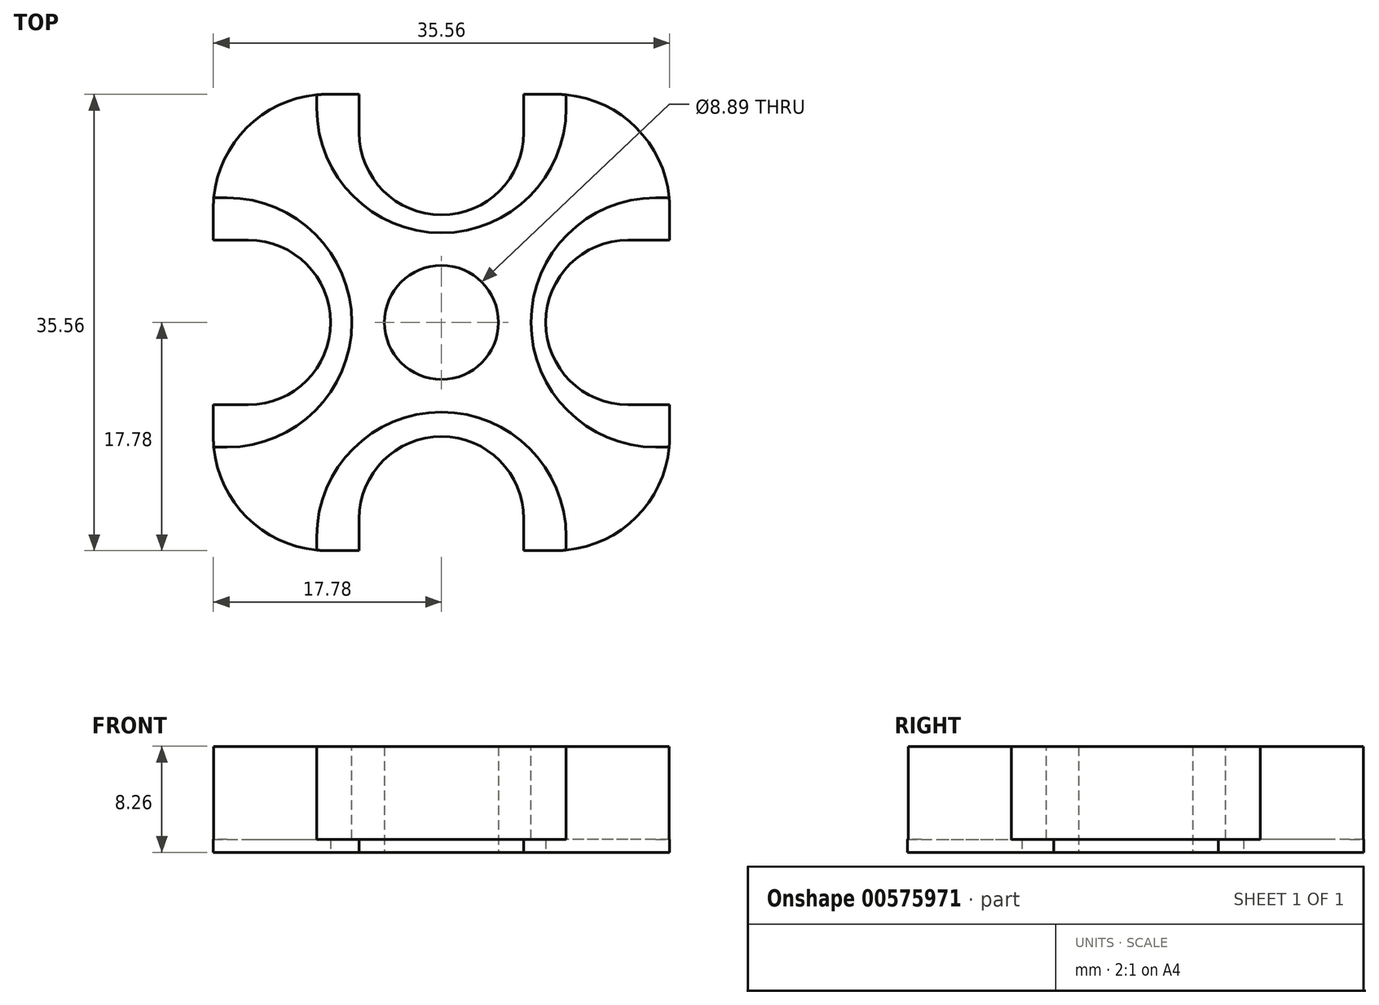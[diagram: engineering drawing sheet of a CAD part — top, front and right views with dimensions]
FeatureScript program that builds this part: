
annotation { "Feature Type Name" : "Feature", "Feature Type Description" : "" }
export const myFeature = defineFeature(function(context is Context, id is Id, definition is map)
    precondition{}
    {
        {
            var Q0;
            Q0=qCreatedBy(makeId("Top.planeOp"),FACE);
            var sketch = newSketch(context, id + "F0", { "sketchPlane" : qUnion([Q0])});
            skLineSegment(sketch, "E0.bottom", {"start": v(17.78, -17.78) * mm, "end": v(-17.78, -17.78) * mm});
            skLineSegment(sketch, "E0.top", {"start": v(17.78, 17.78) * mm, "end": v(-17.78, 17.78) * mm});
            skLineSegment(sketch, "E0.left", {"start": v(17.78, -17.78) * mm, "end": v(17.78, 17.78) * mm});
            skLineSegment(sketch, "E0.right", {"start": v(-17.78, -17.78) * mm, "end": v(-17.78, 17.78) * mm});
            skPoint(sketch, "E0.middle", {"position": v(0, 0) * mm});
            skArc(sketch, "E1", {"start": v(-8.14, -17.78) * mm, "mid": v(0, -23.06) * mm, "end": v(8.14, -17.78) * mm});
            skPoint(sketch, "E2.center.orphan", {"position": v(0, 15.65) * mm});
            skPoint(sketch, "E3.center.orphan", {"position": v(-13.58, 0) * mm});
            skPoint(sketch, "E4.center.orphan", {"position": v(13.88, 0) * mm});
            skSolve(sketch);
        }
        {
            var Q0;
            Q0=makeQuery(id+"F0.imprint","IMPRINT",FACE,{"disambiguationData":[TD([[makeQuery(id+"F0.imprint","IMPRINT",EDGE,{"derivedFrom":sQuery(id+"F0.wireOp",EDGE,"E0.top")}),1.0]])]});
            extrude(context, id + "F1", {"entities" : qUnion([Q0]), "depth" : 8.25 * mm, "offsetDistance" : 25.4 * mm});
        }
        {
            var Q0;
            Q0=makeQuery(id+"F1.opExtrude","CAP_FACE",FACE,{"disambiguationData":[OSD([sQuery(id+"F0.wireOp",EDGE,"E0.bottom"),sQuery(id+"F0.wireOp",EDGE,"E0.top"),sQuery(id+"F0.wireOp",EDGE,"E0.left"),sQuery(id+"F0.wireOp",EDGE,"E0.right")])],"isStart":false});
            var sketch = newSketch(context, id + "F2", { "sketchPlane" : qUnion([Q0])});
            skArc(sketch, "E5", {"start": v(-9.72, 16.7) * mm, "mid": v(0, 6.99) * mm, "end": v(9.72, 16.7) * mm});
            skArc(sketch, "E6", {"start": v(16.7, 9.72) * mm, "mid": v(6.98, 0) * mm, "end": v(16.7, -9.72) * mm});
            skArc(sketch, "E7", {"start": v(-16.7, -9.72) * mm, "mid": v(-6.99, 0) * mm, "end": v(-16.7, 9.72) * mm});
            skArc(sketch, "E8", {"start": v(9.72, -16.7) * mm, "mid": v(0, -6.99) * mm, "end": v(-9.72, -16.7) * mm});
            skLineSegment(sketch, "E9", {"start": v(-9.72, 16.7) * mm, "end": v(-9.72, 17.78) * mm});
            skLineSegment(sketch, "E10", {"start": v(9.72, 16.7) * mm, "end": v(9.72, 17.78) * mm});
            skLineSegment(sketch, "E11", {"start": v(-16.7, 9.72) * mm, "end": v(-17.78, 9.72) * mm});
            skLineSegment(sketch, "E12", {"start": v(-16.7, -9.72) * mm, "end": v(-17.78, -9.72) * mm});
            skLineSegment(sketch, "E13", {"start": v(-9.72, -16.7) * mm, "end": v(-9.72, -17.78) * mm});
            skLineSegment(sketch, "E14", {"start": v(9.72, -16.7) * mm, "end": v(9.72, -17.78) * mm});
            skLineSegment(sketch, "E15", {"start": v(16.7, 9.72) * mm, "end": v(17.78, 9.72) * mm});
            skLineSegment(sketch, "E16", {"start": v(16.7, -9.72) * mm, "end": v(17.78, -9.72) * mm});
            skPoint(sketch, "E17.orphan", {"position": v(-9.66, -17.78) * mm});
            skLineSegment(sketch, "E18", {"start": v(9.72, 17.78) * mm, "end": v(-9.72, 17.78) * mm});
            skLineSegment(sketch, "E19", {"start": v(-17.78, 9.72) * mm, "end": v(-17.78, -9.72) * mm});
            skLineSegment(sketch, "E20", {"start": v(17.78, -9.72) * mm, "end": v(17.78, 9.72) * mm});
            skLineSegment(sketch, "E21", {"start": v(-9.72, -17.78) * mm, "end": v(9.72, -17.78) * mm});
            skSolve(sketch);
        }
        {
            var Q0;
            Q0=qSketchRegion(id+"F2",true);
            extrude(context, id + "F3", {"entities" : qUnion([Q0]), "operationType" : NewBodyOperationType.REMOVE, "oppositeDirection" : true, "depth" : 7.24 * mm, "offsetDistance" : 25.4 * mm});
        }
        {
            var Q0;
            Q0=makeQuery(id+"F1.opExtrude","CAP_FACE",FACE,{"disambiguationData":[OSD([sQuery(id+"F0.wireOp",EDGE,"E0.bottom"),sQuery(id+"F0.wireOp",EDGE,"E0.top"),sQuery(id+"F0.wireOp",EDGE,"E0.left"),sQuery(id+"F0.wireOp",EDGE,"E0.right")])],"isStart":true});
            var sketch = newSketch(context, id + "F4", { "sketchPlane" : qUnion([Q0])});
            skArc(sketch, "E22", {"start": v(-6.41, 15.3) * mm, "mid": v(0, 8.9) * mm, "end": v(6.41, 15.3) * mm});
            skArc(sketch, "E23", {"start": v(14.54, 6.41) * mm, "mid": v(8.13, 0) * mm, "end": v(14.54, -6.41) * mm});
            skArc(sketch, "E24", {"start": v(-15.05, -6.41) * mm, "mid": v(-8.64, 0) * mm, "end": v(-15.05, 6.41) * mm});
            skArc(sketch, "E25", {"start": v(6.41, -14.8) * mm, "mid": v(0, -8.38) * mm, "end": v(-6.41, -14.8) * mm});
            skLineSegment(sketch, "E26", {"start": v(-15.05, 6.41) * mm, "end": v(-17.78, 6.41) * mm});
            skLineSegment(sketch, "E27", {"start": v(-15.05, -6.41) * mm, "end": v(-17.78, -6.41) * mm});
            skLineSegment(sketch, "E28", {"start": v(-6.41, -14.8) * mm, "end": v(-6.41, -17.78) * mm});
            skLineSegment(sketch, "E29", {"start": v(6.41, -14.8) * mm, "end": v(6.41, -17.78) * mm});
            skLineSegment(sketch, "E30", {"start": v(14.54, -6.41) * mm, "end": v(17.78, -6.41) * mm});
            skLineSegment(sketch, "E31", {"start": v(14.54, 6.41) * mm, "end": v(17.78, 6.41) * mm});
            skLineSegment(sketch, "E32", {"start": v(-6.41, 15.3) * mm, "end": v(-6.41, 17.78) * mm});
            skLineSegment(sketch, "E33", {"start": v(6.41, 15.3) * mm, "end": v(6.41, 17.78) * mm});
            skLineSegment(sketch, "E34", {"start": v(-6.41, 17.78) * mm, "end": v(6.41, 17.78) * mm});
            skLineSegment(sketch, "E35", {"start": v(-17.78, 6.41) * mm, "end": v(-17.78, -6.41) * mm});
            skLineSegment(sketch, "E36", {"start": v(-6.41, -17.78) * mm, "end": v(6.41, -17.78) * mm});
            skLineSegment(sketch, "E37", {"start": v(17.78, -6.41) * mm, "end": v(17.78, 6.41) * mm});
            skSolve(sketch);
        }
        {
            var Q0;
            Q0=qSketchRegion(id+"F4",true);
            extrude(context, id + "F5", {"entities" : qUnion([Q0]), "operationType" : NewBodyOperationType.REMOVE, "oppositeDirection" : true, "depth" : 25.4 * mm, "offsetDistance" : 25.4 * mm});
        }
        {
            var Q0;
            Q0=makeQuery(id+"F1.opExtrude","SWEPT_EDGE",EDGE,{"disambiguationData":[OSD([sQuery(id+"F0.wireOp",EDGE,"E0.top"),sQuery(id+"F0.wireOp",EDGE,"E0.right")])]});
            var Q1;
            Q1=makeQuery(id+"F1.opExtrude","SWEPT_EDGE",EDGE,{"disambiguationData":[OSD([sQuery(id+"F0.wireOp",EDGE,"E0.bottom"),sQuery(id+"F0.wireOp",EDGE,"E0.right")])]});
            var Q2;
            Q2=makeQuery(id+"F1.opExtrude","SWEPT_EDGE",EDGE,{"disambiguationData":[OSD([sQuery(id+"F0.wireOp",EDGE,"E0.bottom"),sQuery(id+"F0.wireOp",EDGE,"E0.left")])]});
            var Q3;
            Q3=makeQuery(id+"F1.opExtrude","SWEPT_EDGE",EDGE,{"disambiguationData":[OSD([sQuery(id+"F0.wireOp",EDGE,"E0.top"),sQuery(id+"F0.wireOp",EDGE,"E0.left")])]});
            fillet(context, id + "F6", {"entities" : qUnion([Q0, Q1, Q2, Q3]), "radius" : 8.9 * mm, "tangentPropagation" : true, "allowEdgeOverflow" : false});
        }
        {
            var Q0;
            Q0=makeQuery(id+"F1.opExtrude","CAP_FACE",FACE,{"disambiguationData":[OSD([sQuery(id+"F0.wireOp",EDGE,"E0.bottom"),sQuery(id+"F0.wireOp",EDGE,"E0.top"),sQuery(id+"F0.wireOp",EDGE,"E0.left"),sQuery(id+"F0.wireOp",EDGE,"E0.right")])],"isStart":true});
            var sketch = newSketch(context, id + "F7", { "sketchPlane" : qUnion([Q0])});
            skCircle(sketch, "E38", {"center": v(0, 0) * mm, "radius": 4.45 * mm});
            skSolve(sketch);
        }
        {
            var Q0;
            Q0=qSketchRegion(id+"F7",true);
            extrude(context, id + "F8", {"entities" : qUnion([Q0]), "operationType" : NewBodyOperationType.REMOVE, "oppositeDirection" : true, "depth" : 25.4 * mm, "offsetDistance" : 25.4 * mm});
        }
    });
